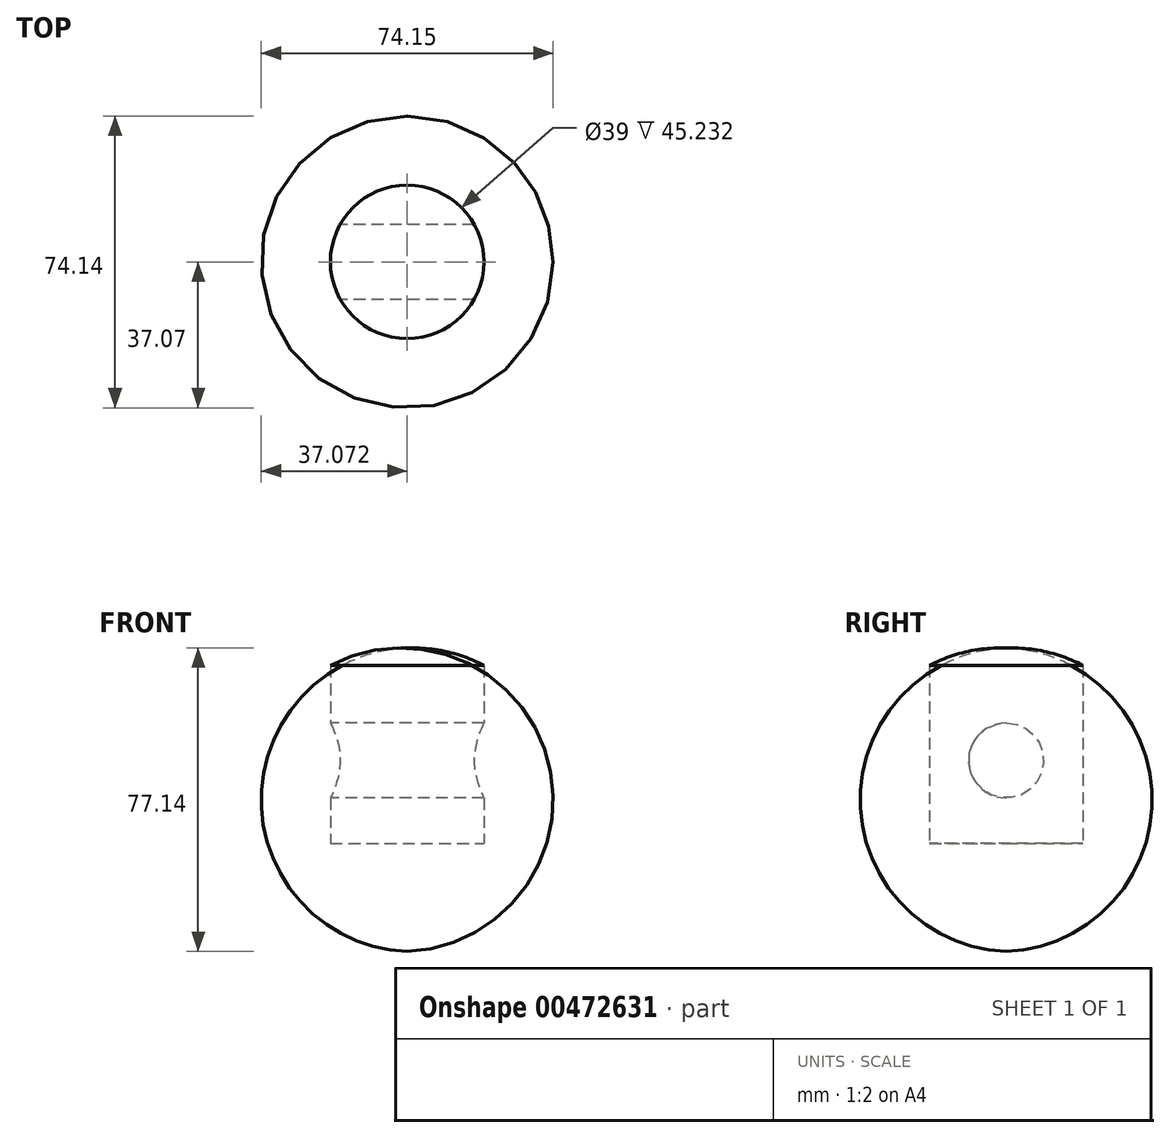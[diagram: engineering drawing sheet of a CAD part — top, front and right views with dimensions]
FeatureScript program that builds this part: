
annotation { "Feature Type Name" : "Feature", "Feature Type Description" : "" }
export const myFeature = defineFeature(function(context is Context, id is Id, definition is map)
    precondition{}
    {
        {
            var Q0;
            Q0=qCreatedBy(makeId("Front.planeOp"),FACE);
            var sketch = newSketch(context, id + "F0", { "sketchPlane" : qUnion([Q0])});
            skLineSegment(sketch, "E0", {"start": v(63.13, 8.44) * mm, "end": v(43.63, 8.44) * mm});
            skLineSegment(sketch, "E1", {"start": v(43.63, 8.44) * mm, "end": v(43.63, 58.1) * mm});
            skLineSegment(sketch, "E2", {"start": v(63.13, 8.44) * mm, "end": v(63.13, 53.68) * mm});
            skArc(sketch, "E3", {"start": v(63.13, 53.68) * mm, "mid": v(53.67, 57.17) * mm, "end": v(43.63, 58.1) * mm});
            skSolve(sketch);
        }
        {
            var Q0;
            Q0 = qSketchRegion(id + "F0", true);
            var Q1;
            Q1=sQuery(id+"F0.wireOp",EDGE,"E1");
            revolve(context, id + "F1", {"entities" : qUnion([Q0]), "axis" : qUnion([Q1]), "revolveType" : RevolveType.FULL});
        }
        {
            var Q0;
            Q0=qCreatedBy(makeId("Right.planeOp"),FACE);
            var sketch = newSketch(context, id + "F2", { "sketchPlane" : qUnion([Q0])});
            skCircle(sketch, "E4", {"center": v(0, 29.55) * mm, "radius": 9.53 * mm});
            skSolve(sketch);
        }
        {
            var Q0;
            Q0=makeQuery(id+"F2.imprint","IMPRINT",FACE,{"disambiguationData":[TD([[makeQuery(id+"F2.imprint","IMPRINT",EDGE,{"derivedFrom":sQuery(id+"F2.wireOp",EDGE,"E4")}),1.0]])]});
            extrude(context, id + "F3", {"entities" : qUnion([Q0]), "operationType" : NewBodyOperationType.REMOVE, "depth" : 223520 * mm});
        }
    });
